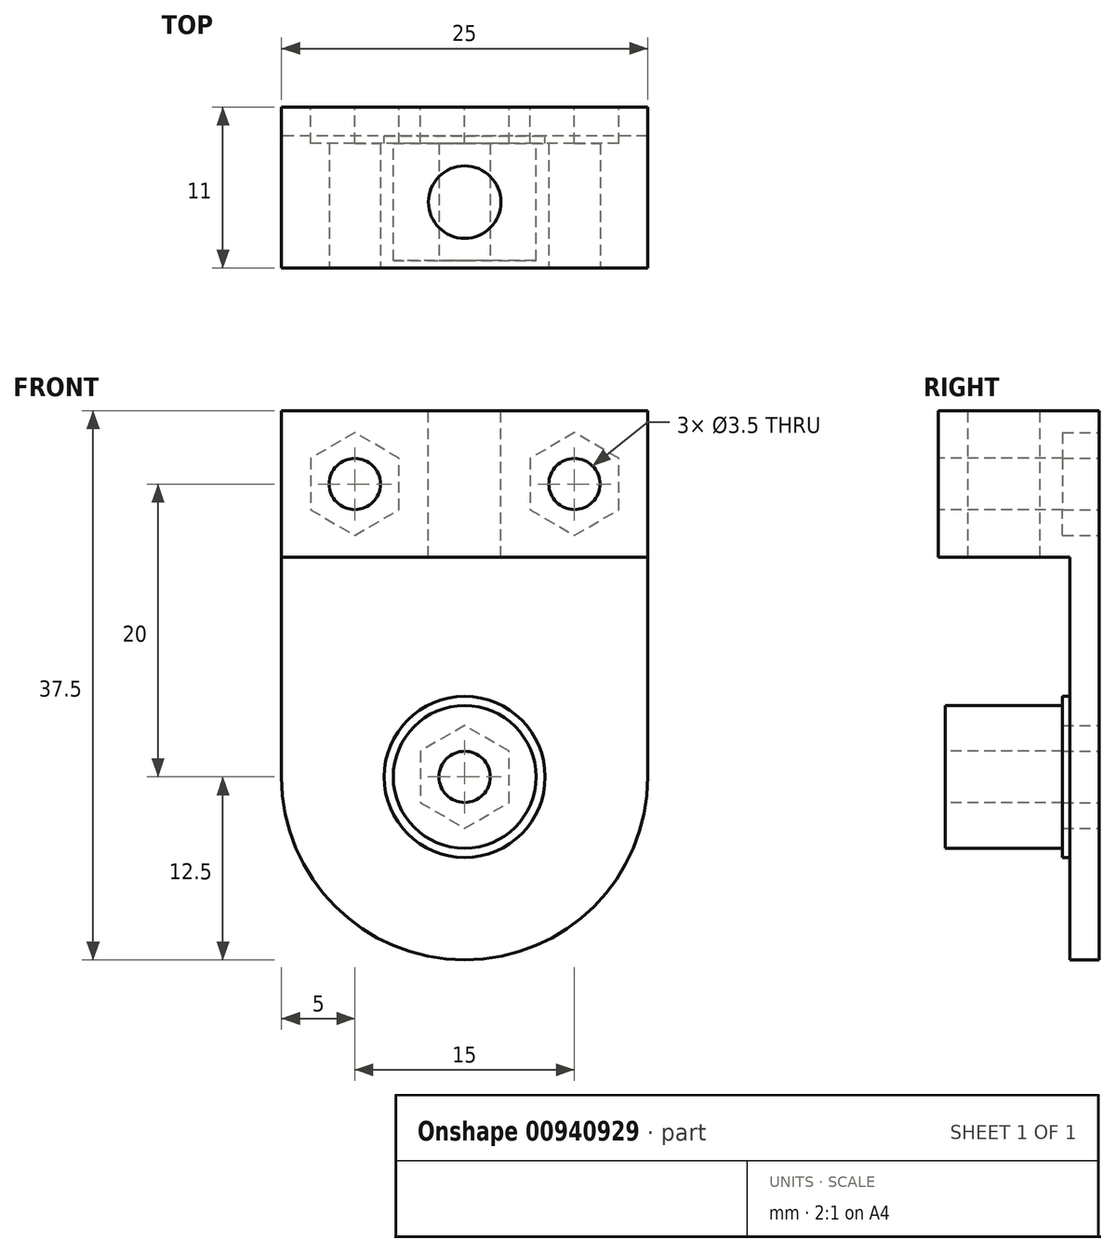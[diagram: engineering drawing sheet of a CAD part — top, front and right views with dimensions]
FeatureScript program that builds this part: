
annotation { "Feature Type Name" : "Feature", "Feature Type Description" : "" }
export const myFeature = defineFeature(function(context is Context, id is Id, definition is map)
    precondition{}
    {
        {
            var Q0;
            Q0=qCreatedBy(makeId("Top.planeOp"),FACE);
            var sketch = newSketch(context, id + "F0", { "sketchPlane" : qUnion([Q0])});
            skLineSegment(sketch, "E0.bottom", {"start": v(12.5, 4.5) * mm, "end": v(-12.5, 4.5) * mm});
            skLineSegment(sketch, "E0.top", {"start": v(12.5, -4.5) * mm, "end": v(-12.5, -4.5) * mm});
            skLineSegment(sketch, "E0.left", {"start": v(12.5, 4.5) * mm, "end": v(12.5, -4.5) * mm});
            skLineSegment(sketch, "E0.right", {"start": v(-12.5, 4.5) * mm, "end": v(-12.5, -4.5) * mm});
            skPoint(sketch, "E0.middle", {"position": v(0, 0) * mm});
            skCircle(sketch, "E1", {"center": v(0, 0) * mm, "radius": 2.48 * mm});
            skSolve(sketch);
        }
        {
            var Q0;
            Q0=qSketchRegion(id+"F0",true);
            extrude(context, id + "F1", {"entities" : qUnion([Q0]), "depth" : -10 * mm, "offsetDistance" : 25 * mm});
        }
        {
            var Q0;
            Q0=makeQuery(id+"F1.opExtrude","SWEPT_FACE",FACE,{"disambiguationData":[OSD([sQuery(id+"F0.wireOp",EDGE,"E0.bottom")])]});
            var sketch = newSketch(context, id + "F2", { "sketchPlane" : qUnion([Q0])});
            skLineSegment(sketch, "E2.bottom", {"start": v(-12.5, 0) * mm, "end": v(12.5, 0) * mm});
            skLineSegment(sketch, "E2.top", {"start": v(-12.5, -25) * mm, "end": v(12.5, -25) * mm});
            skLineSegment(sketch, "E2.left", {"start": v(-12.5, 0) * mm, "end": v(-12.5, -25) * mm});
            skLineSegment(sketch, "E2.right", {"start": v(12.5, 0) * mm, "end": v(12.5, -25) * mm});
            skCircle(sketch, "E3", {"center": v(0, -25) * mm, "radius": 12.5 * mm});
            skCircle(sketch, "E4", {"center": v(0, -25) * mm, "radius": 1.75 * mm});
            skSolve(sketch);
        }
        {
            var Q0;
            Q0=qSketchRegion(id+"F2",true);
            extrude(context, id + "F3", {"entities" : qUnion([Q0]), "operationType" : NewBodyOperationType.ADD, "depth" : 2 * mm, "offsetDistance" : 25 * mm});
        }
        {
            var Q0;
            Q0=makeQuery(id+"F3.opExtrude","CAP_FACE",FACE,{"disambiguationData":[OSD([sQuery(id+"F2.wireOp",EDGE,"E2.bottom"),sQuery(id+"F2.wireOp",EDGE,"E2.left"),sQuery(id+"F2.wireOp",EDGE,"E2.right"),sQuery(id+"F2.wireOp",EDGE,"E3"),sQuery(id+"F2.wireOp",EDGE,"E4")])],"isStart":true});
            var sketch = newSketch(context, id + "F4", { "sketchPlane" : qUnion([Q0])});
            skCircle(sketch, "E5", {"center": v(0, -25) * mm, "radius": 5.5 * mm});
            skCircle(sketch, "E6", {"center": v(0, -25) * mm, "radius": 1.75 * mm});
            skSolve(sketch);
        }
        {
            var Q0;
            Q0=qSketchRegion(id+"F4",true);
            extrude(context, id + "F5", {"entities" : qUnion([Q0]), "operationType" : NewBodyOperationType.ADD, "depth" : 0.5 * mm, "offsetDistance" : 25 * mm});
        }
        {
            var Q0;
            Q0=makeQuery(id+"F5.opExtrude","CAP_FACE",FACE,{"disambiguationData":[OSD([sQuery(id+"F4.wireOp",EDGE,"E5"),sQuery(id+"F4.wireOp",EDGE,"E6")])],"isStart":false});
            var sketch = newSketch(context, id + "F6", { "sketchPlane" : qUnion([Q0])});
            skCircle(sketch, "E7", {"center": v(0, -25) * mm, "radius": 1.75 * mm});
            skCircle(sketch, "E8", {"center": v(0, -25) * mm, "radius": 4.88 * mm});
            skSolve(sketch);
        }
        {
            var Q0;
            Q0=qSketchRegion(id+"F6",true);
            extrude(context, id + "F7", {"entities" : qUnion([Q0]), "operationType" : NewBodyOperationType.ADD, "depth" : 8 * mm, "offsetDistance" : 25 * mm});
        }
        {
            var Q0;
            Q0=makeQuery(id+"F1.opExtrude","SWEPT_FACE",FACE,{"disambiguationData":[OSD([sQuery(id+"F0.wireOp",EDGE,"E0.top")])]});
            var sketch = newSketch(context, id + "F8", { "sketchPlane" : qUnion([Q0])});
            skCircle(sketch, "E9", {"center": v(-7.5, -5) * mm, "radius": 1.75 * mm});
            skCircle(sketch, "E10", {"center": v(7.5, -5) * mm, "radius": 1.75 * mm});
            skSolve(sketch);
        }
        {
            var Q0;
            Q0=qSketchRegion(id+"F8",true);
            extrude(context, id + "F9", {"entities" : qUnion([Q0]), "depth" : -25 * mm, "offsetDistance" : 25 * mm});
        }
        {
            var Q0;
            Q0=makeQuery(id+"F9.opExtrude","SWEPT_BODY",BODY,{"disambiguationData":[OSD([sQuery(id+"F8.wireOp",EDGE,"E10")])]});
            var Q1;
            Q1=makeQuery(id+"F9.opExtrude","SWEPT_BODY",BODY,{"disambiguationData":[OSD([sQuery(id+"F8.wireOp",EDGE,"E9")])]});
            var Q2;
            Q2=makeQuery(id+"F1.opExtrude","SWEPT_BODY",BODY,{"disambiguationData":[OSD([sQuery(id+"F0.wireOp",EDGE,"E0.bottom"),sQuery(id+"F0.wireOp",EDGE,"E0.top"),sQuery(id+"F0.wireOp",EDGE,"E0.left"),sQuery(id+"F0.wireOp",EDGE,"E0.right"),sQuery(id+"F0.wireOp",EDGE,"E1")])]});
            booleanBodies(context, id + "F10", {"operationType" : BooleanOperationType.SUBTRACTION, "tools" : qUnion([Q0, Q1]), "targets" : qUnion([Q2])});
        }
        {
            var Q0;
            Q0=makeQuery(id+"F3.opExtrude","CAP_FACE",FACE,{"disambiguationData":[OSD([sQuery(id+"F2.wireOp",EDGE,"E2.bottom"),sQuery(id+"F2.wireOp",EDGE,"E2.left"),sQuery(id+"F2.wireOp",EDGE,"E2.right"),sQuery(id+"F2.wireOp",EDGE,"E3"),sQuery(id+"F2.wireOp",EDGE,"E4")])],"isStart":false});
            var sketch = newSketch(context, id + "F11", { "sketchPlane" : qUnion([Q0])});
            skCircle(sketch, "E11.cCircle", {"center": v(-7.5, -5) * mm, "radius": 3.5 * mm, "construction": true});
            skLineSegment(sketch, "E11.0", {"start": v(-4.47, -3.25) * mm, "end": v(-4.47, -6.75) * mm});
            skLineSegment(sketch, "E11.1", {"start": v(-4.47, -6.75) * mm, "end": v(-7.5, -8.5) * mm});
            skLineSegment(sketch, "E11.2", {"start": v(-7.5, -8.5) * mm, "end": v(-10.53, -6.75) * mm});
            skLineSegment(sketch, "E11.3", {"start": v(-10.53, -6.75) * mm, "end": v(-10.53, -3.25) * mm});
            skLineSegment(sketch, "E11.4", {"start": v(-10.53, -3.25) * mm, "end": v(-7.5, -1.5) * mm});
            skLineSegment(sketch, "E11.5", {"start": v(-7.5, -1.5) * mm, "end": v(-4.47, -3.25) * mm});
            skCircle(sketch, "E12.cCircle", {"center": v(7.5, -5) * mm, "radius": 3.5 * mm, "construction": true});
            skLineSegment(sketch, "E12.0", {"start": v(10.53, -3.25) * mm, "end": v(10.53, -6.75) * mm});
            skLineSegment(sketch, "E12.1", {"start": v(10.53, -6.75) * mm, "end": v(7.5, -8.5) * mm});
            skLineSegment(sketch, "E12.2", {"start": v(7.5, -8.5) * mm, "end": v(4.47, -6.75) * mm});
            skLineSegment(sketch, "E12.3", {"start": v(4.47, -6.75) * mm, "end": v(4.47, -3.25) * mm});
            skLineSegment(sketch, "E12.4", {"start": v(4.47, -3.25) * mm, "end": v(7.5, -1.5) * mm});
            skLineSegment(sketch, "E12.5", {"start": v(7.5, -1.5) * mm, "end": v(10.53, -3.25) * mm});
            skCircle(sketch, "E13.cCircle", {"center": v(0, -25) * mm, "radius": 3.5 * mm, "construction": true});
            skLineSegment(sketch, "E13.0", {"start": v(3.03, -23.25) * mm, "end": v(3.03, -26.75) * mm});
            skLineSegment(sketch, "E13.1", {"start": v(3.03, -26.75) * mm, "end": v(0, -28.5) * mm});
            skLineSegment(sketch, "E13.2", {"start": v(0, -28.5) * mm, "end": v(-3.03, -26.75) * mm});
            skLineSegment(sketch, "E13.3", {"start": v(-3.03, -26.75) * mm, "end": v(-3.03, -23.25) * mm});
            skLineSegment(sketch, "E13.4", {"start": v(-3.03, -23.25) * mm, "end": v(0, -21.5) * mm});
            skLineSegment(sketch, "E13.5", {"start": v(0, -21.5) * mm, "end": v(3.03, -23.25) * mm});
            skSolve(sketch);
        }
        {
            var Q0;
            Q0 = qSketchRegion(id + "F11", true);
            extrude(context, id + "F12", {"entities" : qUnion([Q0]), "depth" : -2.5 * mm, "offsetDistance" : 25 * mm});
        }
        {
            var Q0;
            Q0=makeQuery(id+"F12.opExtrude","SWEPT_BODY",BODY,{"disambiguationData":[OSD([sQuery(id+"F11.wireOp",EDGE,"E13.0"),sQuery(id+"F11.wireOp",EDGE,"E13.1"),sQuery(id+"F11.wireOp",EDGE,"E13.2"),sQuery(id+"F11.wireOp",EDGE,"E13.3"),sQuery(id+"F11.wireOp",EDGE,"E13.4"),sQuery(id+"F11.wireOp",EDGE,"E13.5")])]});
            var Q1;
            Q1=makeQuery(id+"F12.opExtrude","SWEPT_BODY",BODY,{"disambiguationData":[OSD([sQuery(id+"F11.wireOp",EDGE,"E12.0"),sQuery(id+"F11.wireOp",EDGE,"E12.1"),sQuery(id+"F11.wireOp",EDGE,"E12.2"),sQuery(id+"F11.wireOp",EDGE,"E12.3"),sQuery(id+"F11.wireOp",EDGE,"E12.4"),sQuery(id+"F11.wireOp",EDGE,"E12.5")])]});
            var Q2;
            Q2=makeQuery(id+"F12.opExtrude","SWEPT_BODY",BODY,{"disambiguationData":[OSD([sQuery(id+"F11.wireOp",EDGE,"E11.0"),sQuery(id+"F11.wireOp",EDGE,"E11.1"),sQuery(id+"F11.wireOp",EDGE,"E11.2"),sQuery(id+"F11.wireOp",EDGE,"E11.3"),sQuery(id+"F11.wireOp",EDGE,"E11.4"),sQuery(id+"F11.wireOp",EDGE,"E11.5")])]});
            var Q3;
            Q3=makeQuery(id+"F1.opExtrude","SWEPT_BODY",BODY,{"disambiguationData":[OSD([sQuery(id+"F0.wireOp",EDGE,"E0.bottom"),sQuery(id+"F0.wireOp",EDGE,"E0.top"),sQuery(id+"F0.wireOp",EDGE,"E0.left"),sQuery(id+"F0.wireOp",EDGE,"E0.right"),sQuery(id+"F0.wireOp",EDGE,"E1")])]});
            booleanBodies(context, id + "F13", {"operationType" : BooleanOperationType.SUBTRACTION, "tools" : qUnion([Q0, Q1, Q2]), "targets" : qUnion([Q3])});
        }
    });
